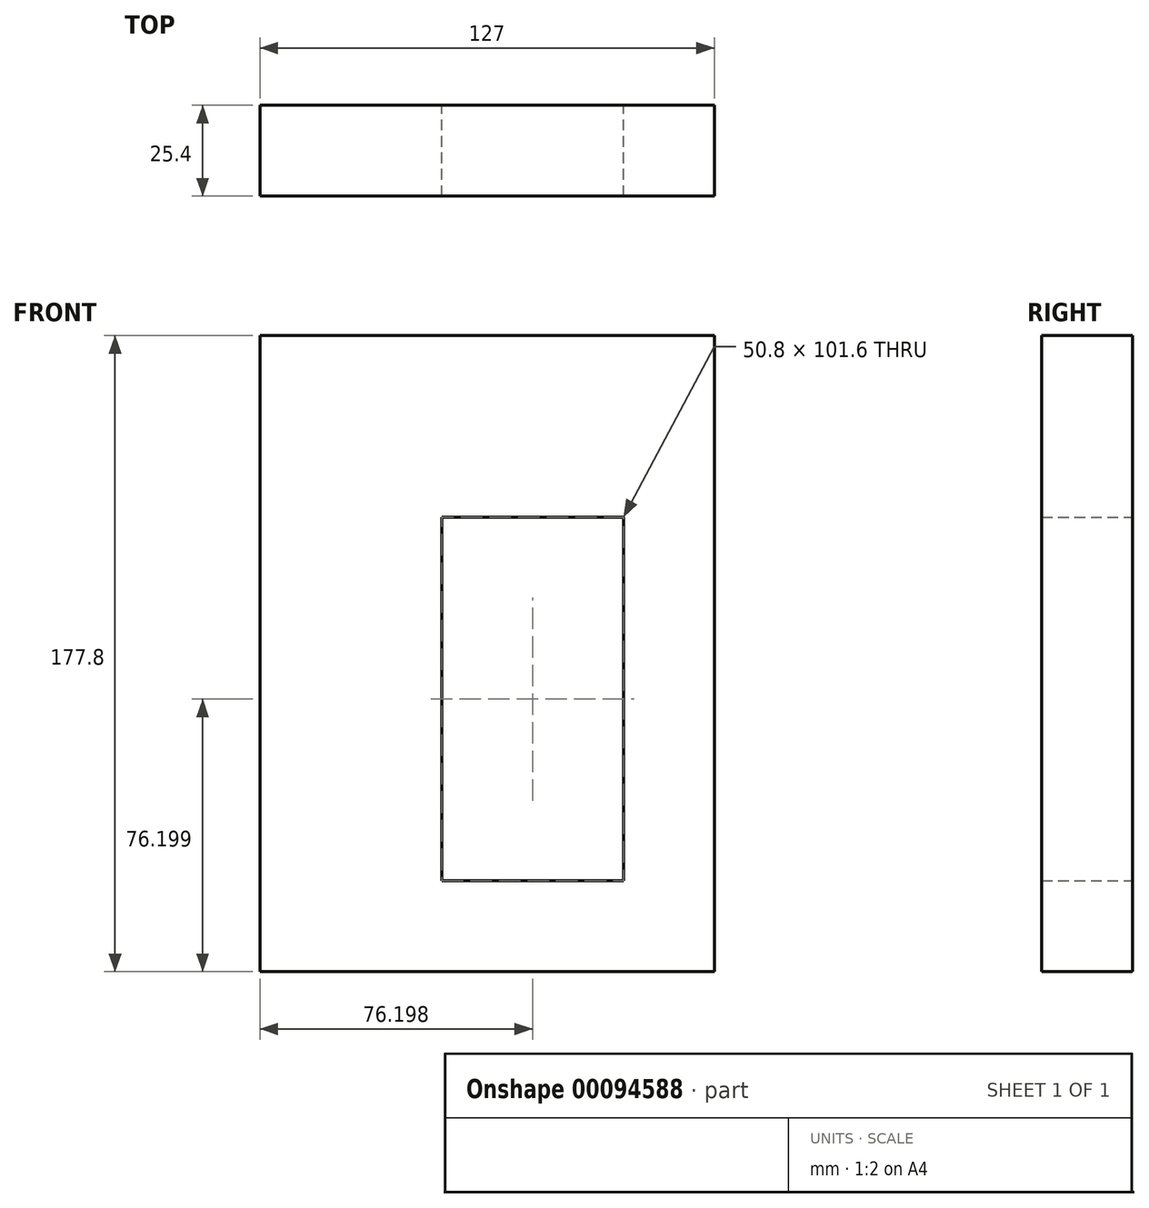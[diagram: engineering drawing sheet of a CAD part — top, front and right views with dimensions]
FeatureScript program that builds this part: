
annotation { "Feature Type Name" : "Feature", "Feature Type Description" : "" }
export const myFeature = defineFeature(function(context is Context, id is Id, definition is map)
    precondition{}
    {
        {
            var Q0;
            Q0=qCreatedBy(makeId("Front.planeOp"),FACE);
            var sketch = newSketch(context, id + "F0", { "sketchPlane" : qUnion([Q0])});
            skLineSegment(sketch, "E0", {"start": v(0.29, -0.1) * mm, "end": v(0.29, 177.7) * mm});
            skLineSegment(sketch, "E1", {"start": v(0.29, 177.7) * mm, "end": v(127.29, 177.7) * mm});
            skLineSegment(sketch, "E2", {"start": v(127.29, 177.7) * mm, "end": v(127.29, -0.1) * mm});
            skLineSegment(sketch, "E3", {"start": v(127.29, -0.1) * mm, "end": v(0.29, -0.1) * mm});
            skLineSegment(sketch, "E4", {"start": v(51.09, 126.9) * mm, "end": v(51.09, 25.3) * mm});
            skLineSegment(sketch, "E5", {"start": v(51.09, 25.3) * mm, "end": v(101.89, 25.3) * mm});
            skLineSegment(sketch, "E6", {"start": v(101.89, 25.3) * mm, "end": v(101.89, 126.9) * mm});
            skLineSegment(sketch, "E7", {"start": v(101.89, 126.9) * mm, "end": v(51.09, 126.9) * mm});
            skSolve(sketch);
        }
        {
            var Q0;
            Q0=makeQuery(id+"F0.imprint","IMPRINT",FACE,{"disambiguationData":[TD([[makeQuery(id+"F0.imprint","IMPRINT",EDGE,{"derivedFrom":sQuery(id+"F0.wireOp",EDGE,"E0")}),-1.0]])]});
            extrude(context, id + "F1", {"entities" : qUnion([Q0]), "depth" : 25.4 * mm});
        }
    });
